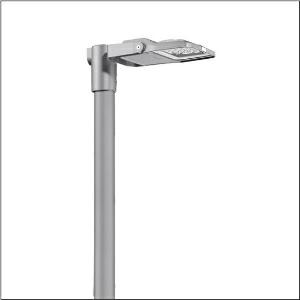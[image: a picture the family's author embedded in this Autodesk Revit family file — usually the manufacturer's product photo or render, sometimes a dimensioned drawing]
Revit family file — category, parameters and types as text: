
# Revit family: floodlight_fl_21_iq_micro___pl43_5xa7761a4a3a_9f97
name_source: partatom
category: Lighting Fixtures
units: mm (PartAtom-declared; Revit-internal decimal feet)

## family parameters
Cut with Voids When Loaded = No
Host = Face
Light Source = No
Part Type = Normal
Room Calculation Point = No
Round Connector Dimension = Use Diameter
Shared = No

## types (1)
- --- (1 x LED, 3170 lm, 23.1 W, 4000K)
    Apparent Load = 23 VA
    CIE Flux Codes = 29 80 99 100 100
    Color Rendering = 70
    Color Temperature = 4000K
    Default Elevation = 1800 mm
    Description = Floodlight FL 21 iQ micro, floodlight, primary light control with lens, of PMMA, primary optical cover: protective disc, of toughened safety glass, transparent, light distribution: PL43, light emission: direct distribution, installation type: surface-mounted, lamps: LED, High Power LED, rated values: 3.170lm | 23,1W | 137,2lm/W (begin service life); end service life: 3.170lm | 23,8W; at 50% lumin. flux: 1.585lm | 11W | 144,1lm/W, colour temperature: 4000K, colour rendering: CRI > 70, light colour: 740, light setting 1 begin service life: 100% | 3.170lm | 23,1W | 137,2lm/W | 4.000K, light setting 1 end service life: 23,8W, further light settings possible, control: optimised constant luminous flux control (CLO 2.0), Desk-Remote (wireless, voltage-free reading and setting of iQ features in the workshop via application-optimized NFC function/RFID function), Light-Fading, Smart-Wire, Night-Set, Lumen-Switch, Temp-Guard, Auto-Match, pre-setting: linear dimming characteristic, with terminal, 6-pole, mains connection: 220..240V, AC, 50/60Hz, luminaire housing, of diecast aluminium, powder-coated, SITECO metallic grey (DB 702S), corrosivity category C5 mid according to DIN EN ISO 12944suitable for swimming poolschlorine-resistant, sealing non-destructively replaceable, please order mast flange separately, mast bracket, of steel, galvanised, powder-coated, SITECO metallic grey (DB 702S), protection rating (complete): IP66, insulation class (complete): insulation class II (safety insulation), certification: CE, ENEC, VDE, protection symbol: D, impact resistance: IK07, permissible operating ambient temperature: -40..+40°C, permissible operating ambient temperature for outdoor applications: -40..+50°C, standard: DIN EN 12944, LABS conformity tested according to VDMA 24364:2018-05, packaging unit: 1 piece

Light Distribution: PL43
    Height = 65 mm
    Lamp = 1 x LED
    Lamp Light Flux = 3170 lm
    Lamp Power = 23.1 W
    Lamp count = 1
    Length = 312 mm
    Luminous efficacy = 137 lm/W
    Manufacturer = Siteco
    ModVariant = No
    Model = 5XA7761A4A3A
    Mounting Place = Pole
    Mounting Type = Pole annexe
    Number of Poles = 1
    OnlyDefault = Yes
    Power Factor = 1
    Product Name = Floodlight FL 21 iQ micro | PL43
    Product group = floodlight | pylon annexe
    ProductGroupID = 6201
    Protection Class = Protection class II
    Protection Degree = IP 66
    RLX_Detail_Level = 1
    RLX_Emergency_Light_Flux = 0 lm
    RLX_Emergency_Type = 0
    RLX_Emergency_Type_DB = No
    RlxData = <blob elided: 102013 chars, md5=0d3fa1ee>
    Socket = socket
    Standby Power = 0 W
    System Light Flux = 3170 lm
    System Power = 23 W
    Type Comments = factory setting: luminous flux: 100 % | dim-lin: 254 | 455 mA
    Type Image = l_1007121.jpg
    URL = http://relux.com
    VarID = @adj_177761
    Voltage = 0 V
    Weight = 0.00 kg
    Width = 230 mm

## geometry (parser evidence)
native form markers: Blend x4, Sweep x11
no freeform markers — native parametric forms only
